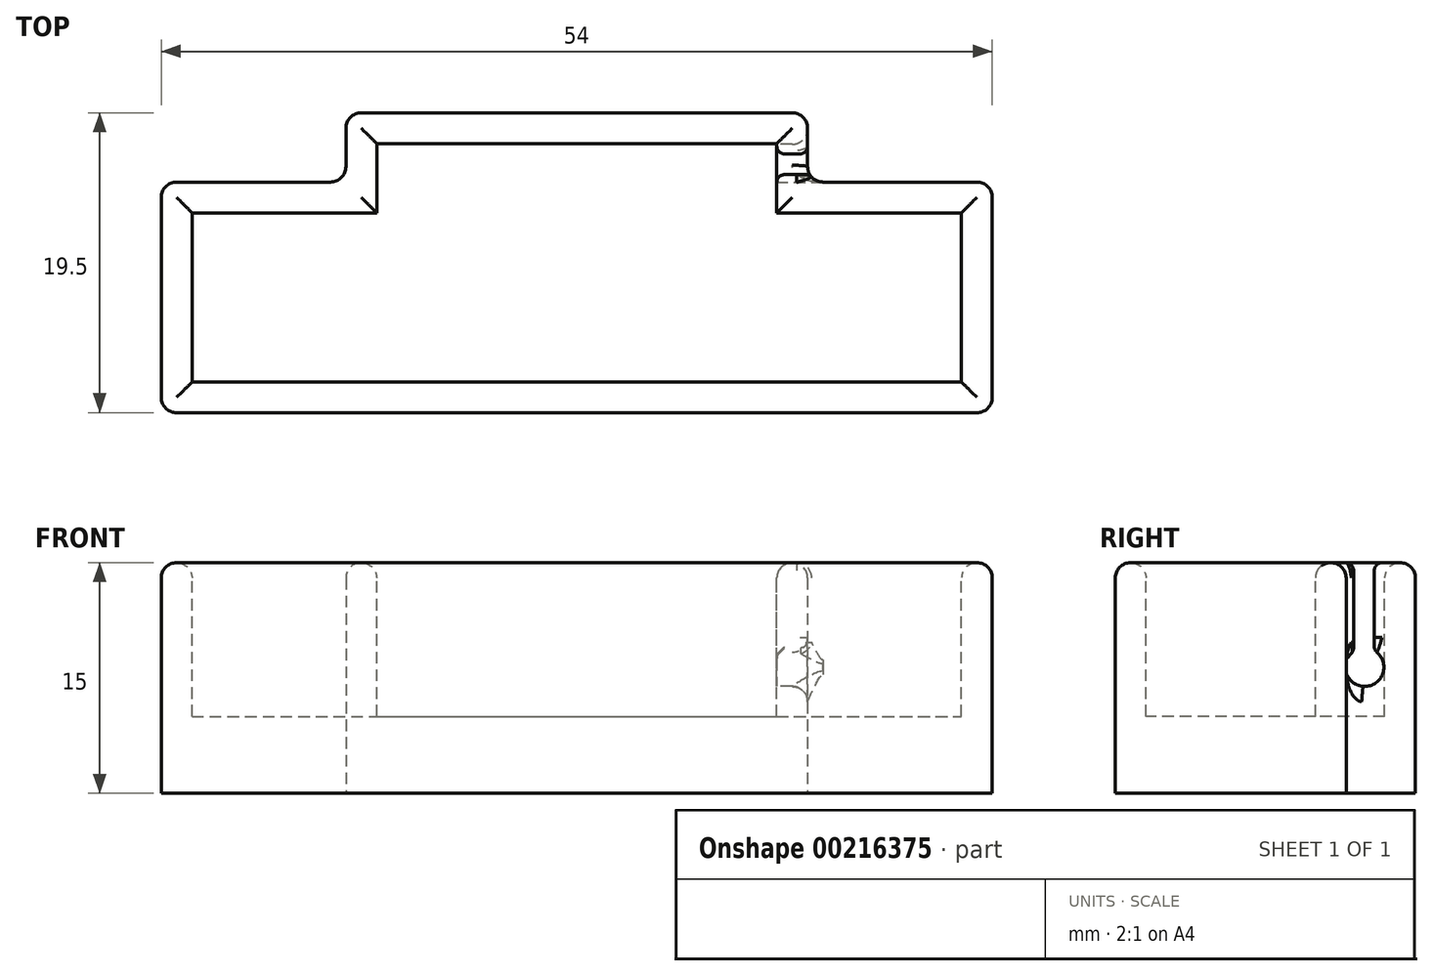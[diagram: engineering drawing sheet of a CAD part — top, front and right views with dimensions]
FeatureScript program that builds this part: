
annotation { "Feature Type Name" : "Feature", "Feature Type Description" : "" }
export const myFeature = defineFeature(function(context is Context, id is Id, definition is map)
    precondition{}
    {
        {
            var Q0;
            Q0=qCreatedBy(makeId("Top.planeOp"),FACE);
            var sketch = newSketch(context, id + "F0", { "sketchPlane" : qUnion([Q0])});
            skLineSegment(sketch, "E0.bottom", {"start": v(-26.47, 10.06) * mm, "end": v(27.53, 10.06) * mm});
            skLineSegment(sketch, "E0.top", {"start": v(-26.47, -4.94) * mm, "end": v(27.53, -4.94) * mm});
            skLineSegment(sketch, "E0.left", {"start": v(-26.47, 10.06) * mm, "end": v(-26.47, -4.94) * mm});
            skLineSegment(sketch, "E0.right", {"start": v(27.53, 10.06) * mm, "end": v(27.53, -4.94) * mm});
            skLineSegment(sketch, "E1.bottom", {"start": v(-14.47, 14.56) * mm, "end": v(15.53, 14.56) * mm});
            skLineSegment(sketch, "E1.top", {"start": v(-14.47, 10.06) * mm, "end": v(15.53, 10.06) * mm});
            skLineSegment(sketch, "E1.left", {"start": v(-14.47, 14.56) * mm, "end": v(-14.47, 10.06) * mm});
            skLineSegment(sketch, "E1.right", {"start": v(15.53, 14.56) * mm, "end": v(15.53, 10.06) * mm});
            skSolve(sketch);
        }
        {
            var Q0;
            {Q0=qUnion([makeQuery(id+"F0.imprint","IMPRINT",FACE,{"disambiguationData":[TD([[makeQuery(id+"F0.imprint","IMPRINT",EDGE,{"derivedFrom":sQuery(id+"F0.wireOp",EDGE,"E0.top")}),1.0]])]}),makeQuery(id+"F0.imprint","IMPRINT",FACE,{"disambiguationData":[TD([[makeQuery(id+"F0.imprint","IMPRINT",EDGE,{"derivedFrom":sQuery(id+"F0.wireOp",EDGE,"E1.bottom")}),-1.0]])]})]);}
            extrude(context, id + "F1", {"entities" : qUnion([Q0]), "depth" : 15 * mm});
        }
        {
            var Q0;
            Q0=makeQuery(id+"F1.opExtrude","CAP_FACE",FACE,{"disambiguationData":[OSD([sQuery(id+"F0.wireOp",EDGE,"E0.bottom"),sQuery(id+"F0.wireOp",EDGE,"E0.top"),sQuery(id+"F0.wireOp",EDGE,"E0.left"),sQuery(id+"F0.wireOp",EDGE,"E0.right"),sQuery(id+"F0.wireOp",EDGE,"E1.bottom"),sQuery(id+"F0.wireOp",EDGE,"E1.left"),sQuery(id+"F0.wireOp",EDGE,"E1.right")])],"isStart":false});
            var sketch = newSketch(context, id + "F2", { "sketchPlane" : qUnion([Q0])});
            skLineSegment(sketch, "E2.bottom", {"start": v(-24.47, 8.06) * mm, "end": v(25.53, 8.06) * mm});
            skLineSegment(sketch, "E2.top", {"start": v(-24.47, -2.94) * mm, "end": v(25.53, -2.94) * mm});
            skLineSegment(sketch, "E2.left", {"start": v(-24.47, 8.06) * mm, "end": v(-24.47, -2.94) * mm});
            skLineSegment(sketch, "E2.right", {"start": v(25.53, 8.06) * mm, "end": v(25.53, -2.94) * mm});
            skLineSegment(sketch, "E3.bottom", {"start": v(-12.47, 12.56) * mm, "end": v(13.53, 12.56) * mm});
            skLineSegment(sketch, "E3.top", {"start": v(-12.47, 8.06) * mm, "end": v(13.53, 8.06) * mm});
            skLineSegment(sketch, "E3.left", {"start": v(-12.47, 12.56) * mm, "end": v(-12.47, 8.06) * mm});
            skLineSegment(sketch, "E3.right", {"start": v(13.53, 12.56) * mm, "end": v(13.53, 8.06) * mm});
            skSolve(sketch);
        }
        {
            var Q0;
            Q0=qSketchRegion(id+"F2",true);
            extrude(context, id + "F3", {"entities" : qUnion([Q0]), "operationType" : NewBodyOperationType.REMOVE, "oppositeDirection" : true, "depth" : 10 * mm});
        }
        {
            var Q0;
            Q0=makeQuery(id+"F1.opExtrude","CAP_FACE",FACE,{"disambiguationData":[OSD([sQuery(id+"F0.wireOp",EDGE,"E0.bottom"),sQuery(id+"F0.wireOp",EDGE,"E0.top"),sQuery(id+"F0.wireOp",EDGE,"E0.left"),sQuery(id+"F0.wireOp",EDGE,"E0.right"),sQuery(id+"F0.wireOp",EDGE,"E1.bottom"),sQuery(id+"F0.wireOp",EDGE,"E1.left"),sQuery(id+"F0.wireOp",EDGE,"E1.right")])],"isStart":false});
            var Q1;
            Q1=makeQuery(id+"F1.opExtrude","CAP_EDGE",EDGE,{"disambiguationData":[OSD([sQuery(id+"F0.wireOp",EDGE,"E0.left")])],"isStart":false});
            var Q2;
            Q2=makeQuery(id+"F3.boolean.opBoolean","COPY",EDGE,{"derivedFrom":makeQuery(id+"F3.opExtrude","CAP_EDGE",EDGE,{"disambiguationData":[OSD([sQuery(id+"F2.wireOp",EDGE,"E2.left")])],"isStart":true})});
            var Q3;
            {var subQ0=sQuery(id+"F2.wireOp",EDGE,"E2.bottom");Q3=makeQuery(id+"F3.boolean.opBoolean","COPY",EDGE,{"derivedFrom":makeQuery(id+"F3.opExtrude","CAP_EDGE",EDGE,{"disambiguationData":[OSD([subQ0]),TDD([makeQuery(id+"F2.imprint","IMPRINT",EDGE,{"disambiguationData":[TD([[makeQuery(id+"F2.imprint","INTERSECT",VERTEX,{"derivedFrom":[subQ0,sQuery(id+"F2.wireOp",EDGE,"E2.left")]}),-1.0]])],"derivedFrom":subQ0})])],"isStart":true})});}
            var Q4;
            {var subQ0=sQuery(id+"F0.wireOp",EDGE,"E0.bottom");Q4=makeQuery(id+"F1.opExtrude","CAP_EDGE",EDGE,{"disambiguationData":[OSD([subQ0]),TDD([makeQuery(id+"F0.imprint","IMPRINT",EDGE,{"disambiguationData":[TD([[makeQuery(id+"F0.imprint","INTERSECT",VERTEX,{"derivedFrom":[subQ0,sQuery(id+"F0.wireOp",EDGE,"E1.left")]}),1.0]])],"derivedFrom":subQ0})])],"isStart":false});}
            var Q5;
            Q5=makeQuery(id+"F1.opExtrude","CAP_EDGE",EDGE,{"disambiguationData":[OSD([sQuery(id+"F0.wireOp",EDGE,"E0.top")])],"isStart":false});
            var Q6;
            Q6=makeQuery(id+"F1.opExtrude","SWEPT_EDGE",EDGE,{"disambiguationData":[OSD([sQuery(id+"F0.wireOp",EDGE,"E0.top"),sQuery(id+"F0.wireOp",EDGE,"E0.left")])]});
            var Q7;
            Q7=makeQuery(id+"F1.opExtrude","SWEPT_EDGE",EDGE,{"disambiguationData":[OSD([sQuery(id+"F0.wireOp",EDGE,"E0.top"),sQuery(id+"F0.wireOp",EDGE,"E0.right")])]});
            var Q8;
            Q8=makeQuery(id+"F1.opExtrude","SWEPT_EDGE",EDGE,{"disambiguationData":[OSD([sQuery(id+"F0.wireOp",EDGE,"E0.bottom"),sQuery(id+"F0.wireOp",EDGE,"E0.left")])]});
            var Q9;
            Q9=makeQuery(id+"F1.opExtrude","CAP_EDGE",EDGE,{"disambiguationData":[OSD([sQuery(id+"F0.wireOp",EDGE,"E0.right")])],"isStart":false});
            var Q10;
            Q10=makeQuery(id+"F1.opExtrude","SWEPT_EDGE",EDGE,{"disambiguationData":[OSD([sQuery(id+"F0.wireOp",EDGE,"E0.bottom"),sQuery(id+"F0.wireOp",EDGE,"E0.right")])]});
            var Q11;
            Q11=makeQuery(id+"F1.opExtrude","SWEPT_EDGE",EDGE,{"disambiguationData":[OSD([sQuery(id+"F0.wireOp",EDGE,"E1.bottom"),sQuery(id+"F0.wireOp",EDGE,"E1.right")])]});
            var Q12;
            Q12=makeQuery(id+"F1.opExtrude","SWEPT_EDGE",EDGE,{"disambiguationData":[OSD([sQuery(id+"F0.wireOp",EDGE,"E1.bottom"),sQuery(id+"F0.wireOp",EDGE,"E1.left")])]});
            var Q13;
            Q13=makeQuery(id+"F1.opExtrude","SWEPT_EDGE",EDGE,{"disambiguationData":[OSD([sQuery(id+"F0.wireOp",EDGE,"E0.bottom"),sQuery(id+"F0.wireOp",EDGE,"E1.left")])]});
            var Q14;
            Q14=makeQuery(id+"F1.opExtrude","SWEPT_EDGE",EDGE,{"disambiguationData":[OSD([sQuery(id+"F0.wireOp",EDGE,"E0.bottom"),sQuery(id+"F0.wireOp",EDGE,"E1.left")])]});
            var Q15;
            Q15=makeQuery(id+"F1.opExtrude","SWEPT_EDGE",EDGE,{"disambiguationData":[OSD([sQuery(id+"F0.wireOp",EDGE,"E0.bottom"),sQuery(id+"F0.wireOp",EDGE,"E1.right")])]});
            fillet(context, id + "F4", {"entities" : qUnion([Q0, Q1, Q2, Q3, Q4, Q5, Q6, Q7, Q8, Q9, Q10, Q11, Q12, Q13, Q14, Q15]), "radius" : 1 * mm, "tangentPropagation" : true, "allowEdgeOverflow" : false});
        }
        {
            var Q0;
            Q0=makeQuery(id+"F3.boolean.opBoolean","COPY",FACE,{"derivedFrom":makeQuery(id+"F3.opExtrude","SWEPT_FACE",FACE,{"disambiguationData":[OSD([sQuery(id+"F2.wireOp",EDGE,"E3.right")])]})});
            var sketch = newSketch(context, id + "F5", { "sketchPlane" : qUnion([Q0])});
            skCircle(sketch, "E4", {"center": v(-11.26, 8.2) * mm, "radius": 1.25 * mm});
            skLineSegment(sketch, "E5.bottom", {"start": v(-10.54, 9.22) * mm, "end": v(-11.89, 9.22) * mm});
            skLineSegment(sketch, "E5.top", {"start": v(-10.54, 15.74) * mm, "end": v(-11.89, 15.74) * mm});
            skLineSegment(sketch, "E5.left", {"start": v(-10.54, 9.22) * mm, "end": v(-10.54, 15.74) * mm});
            skLineSegment(sketch, "E5.right", {"start": v(-11.89, 9.22) * mm, "end": v(-11.89, 15.74) * mm});
            skSolve(sketch);
        }
        {
            var Q0;
            Q0 = qSketchRegion(id + "F5", true);
            extrude(context, id + "F6", {"entities" : qUnion([Q0]), "operationType" : NewBodyOperationType.REMOVE, "oppositeDirection" : true, "depth" : 3 * mm});
        }
        {
            var Q0;
            Q0=makeQuery(id+"F6.boolean.opBoolean","INTERSECT",EDGE,{"derivedFrom":[makeQuery(id+"F1.opExtrude","SWEPT_FACE",FACE,{"disambiguationData":[OSD([sQuery(id+"F0.wireOp",EDGE,"E1.right")])]}),makeQuery(id+"F6.opExtrude","SWEPT_FACE",FACE,{"disambiguationData":[OSD([sQuery(id+"F5.wireOp",EDGE,"E4")])]})]});
            var Q1;
            {var subQ0=sQuery(id+"F0.wireOp",EDGE,"E1.right");var subQ1=sQuery(id+"F0.wireOp",EDGE,"E0.bottom");Q1=makeQuery(id+"F6.boolean.opBoolean","INTERSECT",EDGE,{"disambiguationData":[OD(0.0)],"derivedFrom":[makeQuery(id+"F4.opFillet","BLEND_FACE",FACE,{"disambiguationData":[OSD([subQ1,subQ0]),TDD([makeQuery(id+"F1.opExtrude","SWEPT_EDGE",EDGE,{"disambiguationData":[OSD([subQ1,subQ0])]})])]}),makeQuery(id+"F6.opExtrude","SWEPT_FACE",FACE,{"disambiguationData":[OSD([sQuery(id+"F5.wireOp",EDGE,"E4")])]})]});}
            var Q2;
            {var subQ0=sQuery(id+"F0.wireOp",EDGE,"E1.right");var subQ1=sQuery(id+"F0.wireOp",EDGE,"E0.bottom");Q2=makeQuery(id+"F6.boolean.opBoolean","INTERSECT",EDGE,{"disambiguationData":[OD(1.0)],"derivedFrom":[makeQuery(id+"F4.opFillet","BLEND_FACE",FACE,{"disambiguationData":[OSD([subQ1,subQ0]),TDD([makeQuery(id+"F1.opExtrude","SWEPT_EDGE",EDGE,{"disambiguationData":[OSD([subQ1,subQ0])]})])]}),makeQuery(id+"F6.opExtrude","SWEPT_FACE",FACE,{"disambiguationData":[OSD([sQuery(id+"F5.wireOp",EDGE,"E4")])]})]});}
            fillet(context, id + "F7", {"entities" : qUnion([Q0, Q1, Q2]), "radius" : 1 * mm, "tangentPropagation" : true, "allowEdgeOverflow" : false});
        }
        {
            var Q0;
            Q0=makeQuery(id+"F6.boolean.opBoolean","INTERSECT",EDGE,{"derivedFrom":[makeQuery(id+"F1.opExtrude","SWEPT_FACE",FACE,{"disambiguationData":[OSD([sQuery(id+"F0.wireOp",EDGE,"E1.right")])]}),makeQuery(id+"F6.opExtrude","SWEPT_FACE",FACE,{"disambiguationData":[OSD([sQuery(id+"F5.wireOp",EDGE,"E5.right")])]})]});
            var Q1;
            {var subQ0=sQuery(id+"F0.wireOp",EDGE,"E1.right");var subQ1=sQuery(id+"F0.wireOp",EDGE,"E0.bottom");Q1=makeQuery(id+"F6.boolean.opBoolean","INTERSECT",EDGE,{"derivedFrom":[makeQuery(id+"F4.opFillet","BLEND_FACE",FACE,{"disambiguationData":[OSD([subQ1,subQ0]),TDD([makeQuery(id+"F1.opExtrude","SWEPT_EDGE",EDGE,{"disambiguationData":[OSD([subQ1,subQ0])]})])]}),makeQuery(id+"F6.opExtrude","SWEPT_FACE",FACE,{"disambiguationData":[OSD([sQuery(id+"F5.wireOp",EDGE,"E5.left")])]})]});}
            var Q2;
            Q2=makeQuery(id+"F6.boolean.opBoolean","INTERSECT",EDGE,{"derivedFrom":[makeQuery(id+"F4.opFillet","BLEND_FACE",FACE,{"disambiguationData":[OSD([sQuery(id+"F0.wireOp",EDGE,"E1.right")])]}),makeQuery(id+"F6.opExtrude","SWEPT_FACE",FACE,{"disambiguationData":[OSD([sQuery(id+"F5.wireOp",EDGE,"E5.right")])]})]});
            var Q3;
            {var subQ0=sQuery(id+"F0.wireOp",EDGE,"E1.right");var subQ1=sQuery(id+"F0.wireOp",EDGE,"E0.bottom");Q3=makeQuery(id+"F6.boolean.opBoolean","INTERSECT",EDGE,{"derivedFrom":[makeQuery(id+"F4.opFillet","BLEND_FACE",FACE,{"disambiguationData":[OSD([subQ1,subQ0]),TDD([makeQuery(id+"F1.opExtrude","CAP_VERTEX",VERTEX,{"disambiguationData":[OSD([subQ1,subQ0])],"isStart":false})])]}),makeQuery(id+"F6.opExtrude","SWEPT_FACE",FACE,{"disambiguationData":[OSD([sQuery(id+"F5.wireOp",EDGE,"E5.left")])]})]});}
            var Q4;
            Q4=makeQuery(id+"F6.boolean.opBoolean","INTERSECT",EDGE,{"derivedFrom":[makeQuery(id+"F4.opFillet","BLEND_FACE",FACE,{"disambiguationData":[OSD([sQuery(id+"F0.wireOp",EDGE,"E1.right")])]}),makeQuery(id+"F6.opExtrude","SWEPT_FACE",FACE,{"disambiguationData":[OSD([sQuery(id+"F5.wireOp",EDGE,"E5.left")])]})]});
            var Q5;
            Q5=makeQuery(id+"F6.boolean.opBoolean","COPY",EDGE,{"derivedFrom":makeQuery(id+"F6.opExtrude","CAP_EDGE",EDGE,{"disambiguationData":[OSD([sQuery(id+"F5.wireOp",EDGE,"E5.left")])],"isStart":true})});
            var Q6;
            Q6=makeQuery(id+"F6.boolean.opBoolean","COPY",EDGE,{"derivedFrom":makeQuery(id+"F6.opExtrude","CAP_EDGE",EDGE,{"disambiguationData":[OSD([sQuery(id+"F5.wireOp",EDGE,"E5.right")])],"isStart":true})});
            var Q7;
            Q7=makeQuery(id+"F6.boolean.opBoolean","COPY",EDGE,{"derivedFrom":makeQuery(id+"F6.opExtrude","CAP_EDGE",EDGE,{"disambiguationData":[OSD([sQuery(id+"F5.wireOp",EDGE,"E4")])],"isStart":true})});
            fillet(context, id + "F8", {"entities" : qUnion([Q0, Q1, Q2, Q3, Q4, Q5, Q6, Q7]), "radius" : .5 * mm, "tangentPropagation" : true, "allowEdgeOverflow" : false});
        }
    });
